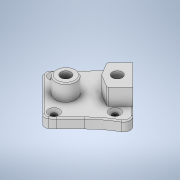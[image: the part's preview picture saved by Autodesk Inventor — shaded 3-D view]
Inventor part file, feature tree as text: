
AUTODESK INVENTOR PART (.ipt)
format: ipt  version: 2020.3 (Build 243373000, 373)  size: 397,312 bytes
history: native  units: mm
features: sketch x4, extrude x4, hole x4, fillet x2, projected_geometry x1
ambient origin geometry x8: Origin, YZ Plane, XZ Plane, XY Plane, X Axis, Y Axis, Z Axis, Center Point
bodies: Body1 (feature_tree)
feature tree (15):
  sketch  "Sketch1"  dims[d0=135.0deg d4=24.6mm]
  extrude  "Extrusion12"  Depth=24.6mm
  extrude  "Extrusion13"  Depth=12.4mm
  extrude  "Extrusion14"  Depth=8.5mm
  extrude  "Extrusion15"  Depth=6.0mm
  sketch  "Sketch3"  dims[d7=60.0mm d9=8.5mm]
  fillet  "Fillet10"  Radius=2.0mm
  fillet  "Fillet11"  Radius=2.0mm
  hole  "Hole3"  [1 undecoded]
  hole  "Hole5"  [1 undecoded]
  hole  "Hole6"  [1 undecoded]
  hole  "Hole7"  [1 undecoded]
  sketch  "Sketch2"  dims[d5=12.4mm d6=70.0mm]
  projected_geometry  "Projected Loop1"
  sketch  "Sketch5"  dims[d10=135.0deg d12=6.0mm d13=2.0mm d14=2.0mm d16=20.0mm d23=6.0mm d29=130.0mm d32=15.0mm d33=4.0mm d34=28.4mm d38=4.0mm d40=6.8mm d49=30.0mm d50=84.0mm d51=3.0mm d52=3.0mm d53=1.5mm d54=20.0mm d59=1.0mm d60=90.0mm d61=135.0deg d70=135.0deg d82=0.7mm d83=0.7mm d84=0.7mm d85=0.7mm d86=6.0mm d102=4.0mm d103=0.0mm d104=4.0mm d105=0.0mm d106=10.9mm d107=0.0mm d108=18.0mm d116=2.0mm d117=0.5mm d118=4.2mm d119=6.0mm d120=7.2mm d121=1.6mm d122=90.0deg d123=5.0mm d124=0.0mm d125=10.9mm d126=0.0mm d134=5.7mm d135=7.2mm d136=4.2mm d137=6.0mm d138=5.6mm d139=0.85mm d140=90.0deg d141=8.0mm d142=0.0mm d143=5.6mm d152=5.6mm d153=6.0mm d154=9.0mm d155=1.0mm d156=90.0deg d157=6.5mm d158=0.0mm d159=2.3mm d160=6.0mm d161=4.5mm d162=0.8mm d163=90.0deg d164=6.5mm d165=0.0mm d166=2.0mm d167=2.0mm d127=0.0625mm d128=0.75mm d129=0.375mm]
note: 4 required parameter values undecoded (feature->parameter linkage not recoverable at this tier; creation-order binding heuristic only, values carry confidence <= 0.55)
